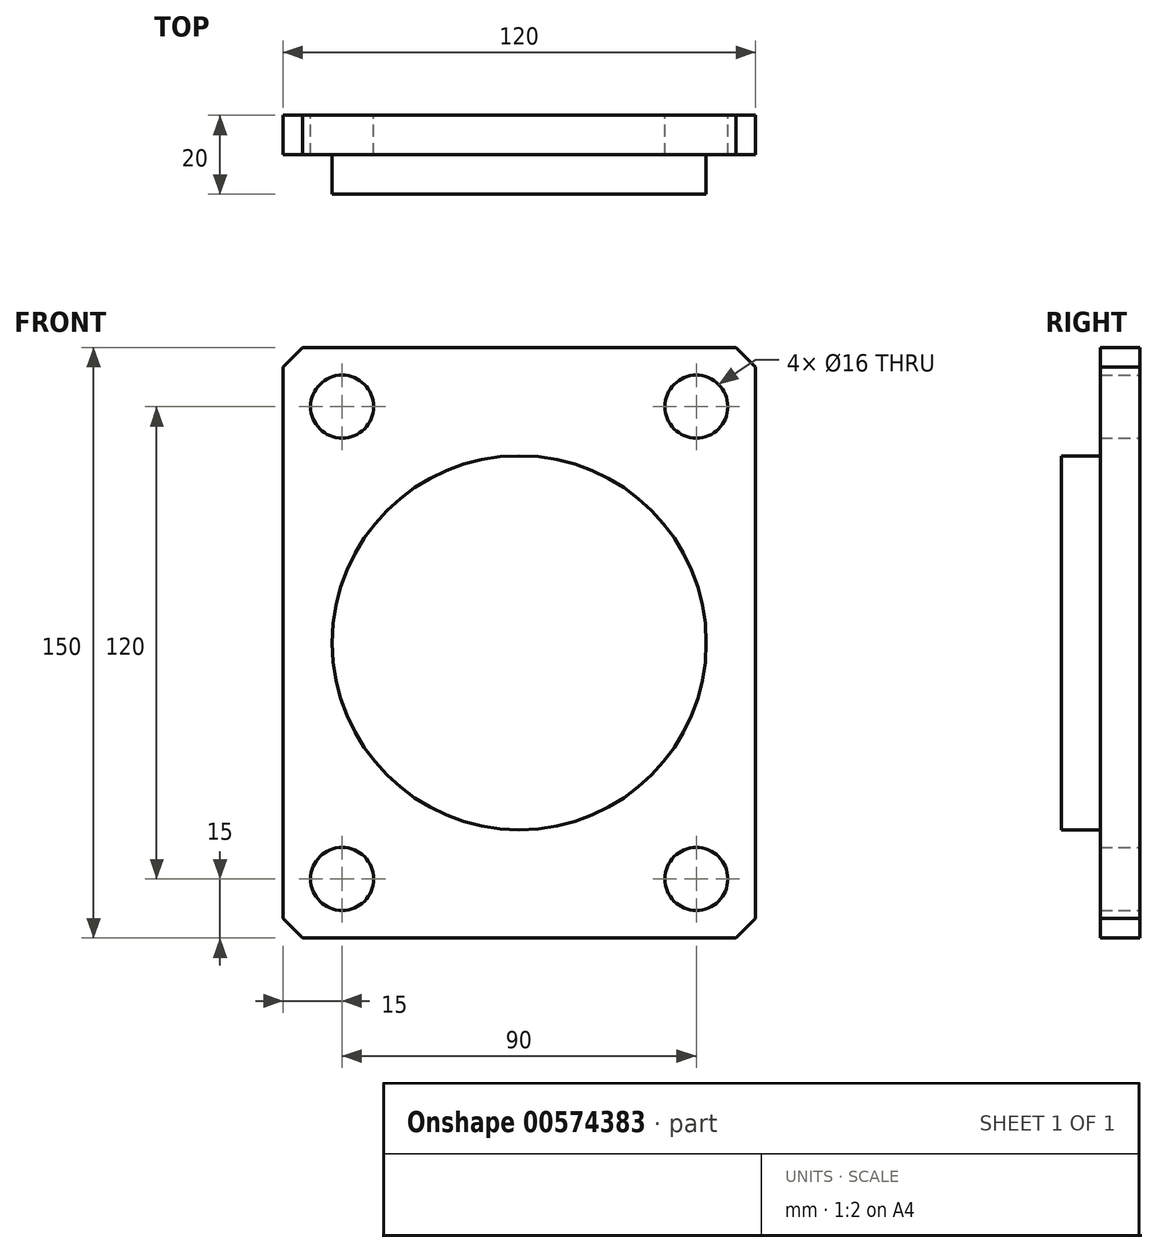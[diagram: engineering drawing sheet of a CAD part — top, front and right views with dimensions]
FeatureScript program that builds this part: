
annotation { "Feature Type Name" : "Feature", "Feature Type Description" : "" }
export const myFeature = defineFeature(function(context is Context, id is Id, definition is map)
    precondition{}
    {
        {
            var Q0;
            Q0=qCreatedBy(makeId("Front.planeOp"),FACE);
            var sketch = newSketch(context, id + "F0", { "sketchPlane" : qUnion([Q0])});
            skLineSegment(sketch, "E0.bottom", {"start": v(-60, 75) * mm, "end": v(60, 75) * mm});
            skLineSegment(sketch, "E0.top", {"start": v(-60, -75) * mm, "end": v(60, -75) * mm});
            skLineSegment(sketch, "E0.left", {"start": v(-60, 75) * mm, "end": v(-60, -75) * mm});
            skLineSegment(sketch, "E0.right", {"start": v(60, 75) * mm, "end": v(60, -75) * mm});
            skLineSegment(sketch, "E1.bottom", {"start": v(-45, 60) * mm, "end": v(45, 60) * mm, "construction": true});
            skLineSegment(sketch, "E1.top", {"start": v(-45, -60) * mm, "end": v(45, -60) * mm, "construction": true});
            skLineSegment(sketch, "E1.left", {"start": v(-45, 60) * mm, "end": v(-45, -60) * mm, "construction": true});
            skLineSegment(sketch, "E1.right", {"start": v(45, 60) * mm, "end": v(45, -60) * mm, "construction": true});
            skCircle(sketch, "E2", {"center": v(-45, 60) * mm, "radius": 8 * mm});
            skCircle(sketch, "E3", {"center": v(45, 60) * mm, "radius": 8 * mm});
            skCircle(sketch, "E4", {"center": v(-45, -60) * mm, "radius": 8 * mm});
            skCircle(sketch, "E5", {"center": v(45, -60) * mm, "radius": 8 * mm});
            skCircle(sketch, "E6", {"center": v(0, 0) * mm, "radius": 47.5 * mm});
            skCircle(sketch, "E7", {"center": v(0, 0) * mm, "radius": 35 * mm});
            skSolve(sketch);
        }
        {
            var Q0;
            Q0=makeQuery(id+"F0.imprint","IMPRINT",FACE,{"disambiguationData":[TD([[makeQuery(id+"F0.imprint","IMPRINT",EDGE,{"derivedFrom":sQuery(id+"F0.wireOp",EDGE,"E6")}),1.0]])]});
            extrude(context, id + "F1", {"entities" : qUnion([Q0]), "depth" : 20 * mm, "offsetDistance" : 25 * mm});
        }
        {
            var Q0;
            Q0 = qSketchRegion(id + "F0", true);
            var Q1;
            Q1=makeQuery(id+"F0.imprint","IMPRINT",FACE,{"disambiguationData":[TD([[makeQuery(id+"F0.imprint","IMPRINT",EDGE,{"derivedFrom":sQuery(id+"F0.wireOp",EDGE,"E7")}),1.0]])]});
            extrude(context, id + "F2", {"entities" : qUnion([Q0, Q1]), "operationType" : NewBodyOperationType.ADD, "depth" : 10 * mm, "offsetDistance" : 25 * mm});
        }
        {
            var Q0;
            Q0=makeQuery(id+"F2.opExtrude","CAP_FACE",FACE,{"disambiguationData":[OSD([sQuery(id+"F0.wireOp",EDGE,"E7")])],"isStart":false});
            extrude(context, id + "F3", {"entities" : qUnion([Q0]), "operationType" : NewBodyOperationType.ADD, "depth" : 10 * mm, "offsetDistance" : 25 * mm});
        }
        {
            var Q0;
            Q0=makeQuery(id+"F2.opExtrude","SWEPT_EDGE",EDGE,{"disambiguationData":[OSD([sQuery(id+"F0.wireOp",EDGE,"E0.bottom"),sQuery(id+"F0.wireOp",EDGE,"E0.left")])]});
            var Q1;
            Q1=makeQuery(id+"F2.opExtrude","SWEPT_EDGE",EDGE,{"disambiguationData":[OSD([sQuery(id+"F0.wireOp",EDGE,"E0.bottom"),sQuery(id+"F0.wireOp",EDGE,"E0.right")])]});
            var Q2;
            Q2=makeQuery(id+"F2.opExtrude","SWEPT_EDGE",EDGE,{"disambiguationData":[OSD([sQuery(id+"F0.wireOp",EDGE,"E0.top"),sQuery(id+"F0.wireOp",EDGE,"E0.right")])]});
            var Q3;
            Q3=makeQuery(id+"F2.opExtrude","SWEPT_EDGE",EDGE,{"disambiguationData":[OSD([sQuery(id+"F0.wireOp",EDGE,"E0.top"),sQuery(id+"F0.wireOp",EDGE,"E0.left")])]});
            chamfer(context, id + "F4", {"entities" : qUnion([Q0, Q1, Q2, Q3]), "width" : 5 * mm, "tangentPropagation" : true});
        }
    });
